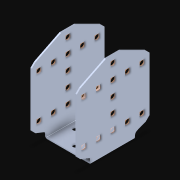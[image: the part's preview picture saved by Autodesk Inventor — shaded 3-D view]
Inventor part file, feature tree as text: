
AUTODESK INVENTOR PART (.ipt)
format: ipt  version: 2021 (Build 250183000, 183)  size: 352,256 bytes
history: native  units: in
note: dims shown in document units (in); Inventor stores cm internally (conversion verified against a paired STEP export)
features: other x27, extrude x26, pattern_linear x8, sketch x2, imported_body x1
ambient origin geometry x8: Origin, YZ Plane, XZ Plane, XY Plane, X Axis, Y Axis, Z Axis, Center Point
bodies: Body1 (feature_tree), Body2 (feature_tree), Body3 (feature_tree), Body4 (feature_tree), Body5 (feature_tree), Body6 (feature_tree), Body7 (feature_tree), Body8 (feature_tree), Body9 (feature_tree), Body10 (feature_tree), Body11 (feature_tree), Body12 (feature_tree), Body13 (feature_tree), Body14 (feature_tree), Body15 (feature_tree), Body16 (feature_tree), Body17 (feature_tree), Body18 (feature_tree), Body19 (feature_tree), Body20 (feature_tree), Body21 (feature_tree), Body22 (feature_tree), Body23 (feature_tree), Body24 (feature_tree), Body25 (feature_tree), Body26 (feature_tree), Body27 (feature_tree)
feature tree (64):
  parser-record x1  (decoder bookkeeping rows leaked as tree rows — omitted from the tree; the rows remain in map.json)
  imported_body  "Base1"
  pattern_linear  "Rectangular Pattern1"  Count1=5 Spacing1=0.5in
  pattern_linear  "Rectangular Pattern2"  Count1=2 Spacing1=0.5in
  pattern_linear  "Rectangular Pattern3"  Count1=2 Spacing1=1.5in
  pattern_linear  "Rectangular Pattern4"  Count1=2 Spacing1=1.5in
  pattern_linear  "Rectangular Pattern5"  Spacing1=0.046in  [1 undecoded]
  pattern_linear  "Rectangular Pattern6"  Count1=5 Spacing1=0.5in
  pattern_linear  "Rectangular Pattern7"  Spacing1=0.046in  [1 undecoded]
  pattern_linear  "Rectangular Pattern8"  Count1=2 Spacing1=0.5in
  other  "Srf1"
  other  "Srf2"
  other  "Srf3"
  other  "Srf4"
  other  "Srf5"
  other  "Srf6"
  other  "Srf7"
  other  "Srf8"
  other  "Srf9"
  other  "Srf10"
  other  "Srf11"
  other  "Srf12"
  other  "Srf13"
  sketch  "Sketch3"  dims[d45=0.046in d46=0.0in d47=1.9685in d49=0.5in]
  other  "Srf14"
  other  "Srf15"
  other  "Srf16"
  other  "Srf17"
  other  "Srf18"
  sketch  "Sketch4"  dims[d51=0.046in d52=0.0in d53=0.7874in d55=0.5in d56=0.7874in d58=1.5in d59=0.7874in d61=1.5in d63=0.046in d64=0.0in d65=1.9685in d67=0.5in d69=0.046in d70=0.0in d71=0.7874in d73=0.5in d74=0.7874in d76=1.5in d77=0.7874in d79=1.5in]
  other  "Srf19"
  other  "Srf20"
  other  "Srf21"
  other  "Srf22"
  other  "Srf23"
  other  "Srf24"
  other  "Srf25"
  other  "Srf26"
  extrude  "ExtrusionSrf1"  Depth=1.5in
  extrude  "ExtrusionSrf6"  Depth=1.5in
  extrude  "ExtrusionSrf14"  [1 undecoded]
  extrude  "ExtrusionSrf19"  [1 undecoded]
  extrude  "ExtrusionSrf2"  [1 undecoded]
  extrude  "ExtrusionSrf3"  [1 undecoded]
  extrude  "ExtrusionSrf4"  [1 undecoded]
  extrude  "ExtrusionSrf5"  [1 undecoded]
  extrude  "ExtrusionSrf7"  [1 undecoded]
  extrude  "ExtrusionSrf8"  [1 undecoded]
  extrude  "ExtrusionSrf9"  [1 undecoded]
  extrude  "ExtrusionSrf10"  [1 undecoded]
  extrude  "ExtrusionSrf11"  [1 undecoded]
  extrude  "ExtrusionSrf12"  [1 undecoded]
  extrude  "ExtrusionSrf13"  [1 undecoded]
  extrude  "ExtrusionSrf15"  [1 undecoded]
  extrude  "ExtrusionSrf16"  [1 undecoded]
  extrude  "ExtrusionSrf17"  [1 undecoded]
  extrude  "ExtrusionSrf18"  [1 undecoded]
  extrude  "ExtrusionSrf20"  [1 undecoded]
  extrude  "ExtrusionSrf21"  [1 undecoded]
  extrude  "ExtrusionSrf22"  [1 undecoded]
  extrude  "ExtrusionSrf23"  [1 undecoded]
  extrude  "ExtrusionSrf24"  [1 undecoded]
  extrude  "ExtrusionSrf25"  [1 undecoded]
  extrude  "ExtrusionSrf26"  [1 undecoded]
note: 26 required parameter values undecoded (feature->parameter linkage not recoverable at this tier; creation-order binding heuristic only, values carry confidence <= 0.55)
